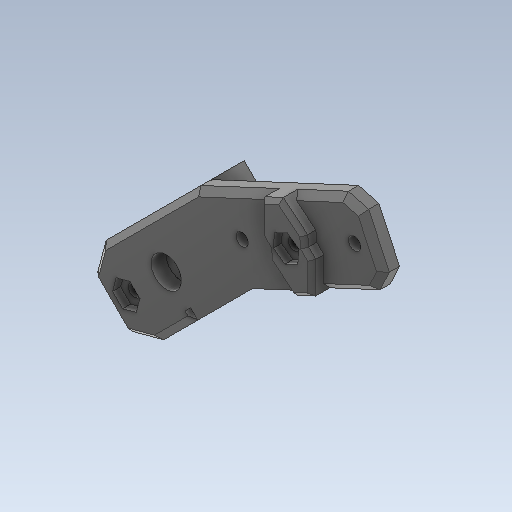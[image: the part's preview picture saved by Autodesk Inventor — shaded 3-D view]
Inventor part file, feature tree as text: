
AUTODESK INVENTOR PART (.ipt)
format: ipt  version: 2020 (Build 240168000, 168)  size: 294,400 bytes
history: native  units: in
note: dims shown in document units (in); Inventor stores cm internally (conversion verified against a paired STEP export)
features: sketch x13, other x3
ambient origin geometry x8: Origin, YZ Plane, XZ Plane, XY Plane, X Axis, Y Axis, Z Axis, Center Point
bodies: Solid1 (feature_tree)
feature tree (16):
  other  "TibiaBot.ipt"
  other  "Solid1::TibiaBot.ipt"
  other  "TaggingFeature1"
  sketch  "Sketch1"  dims[d0=0.3937in]
  sketch  "Sketch9"
  sketch  "Sketch10"
  sketch  "Sketch11"
  sketch  "Sketch15"
  sketch  "Sketch25"
  sketch  "Sketch26"
  sketch  "Sketch8"
  sketch  "Sketch12"
  sketch  "Sketch13"
  sketch  "Sketch19"
  sketch  "Sketch20"
  sketch  "Sketch21"
